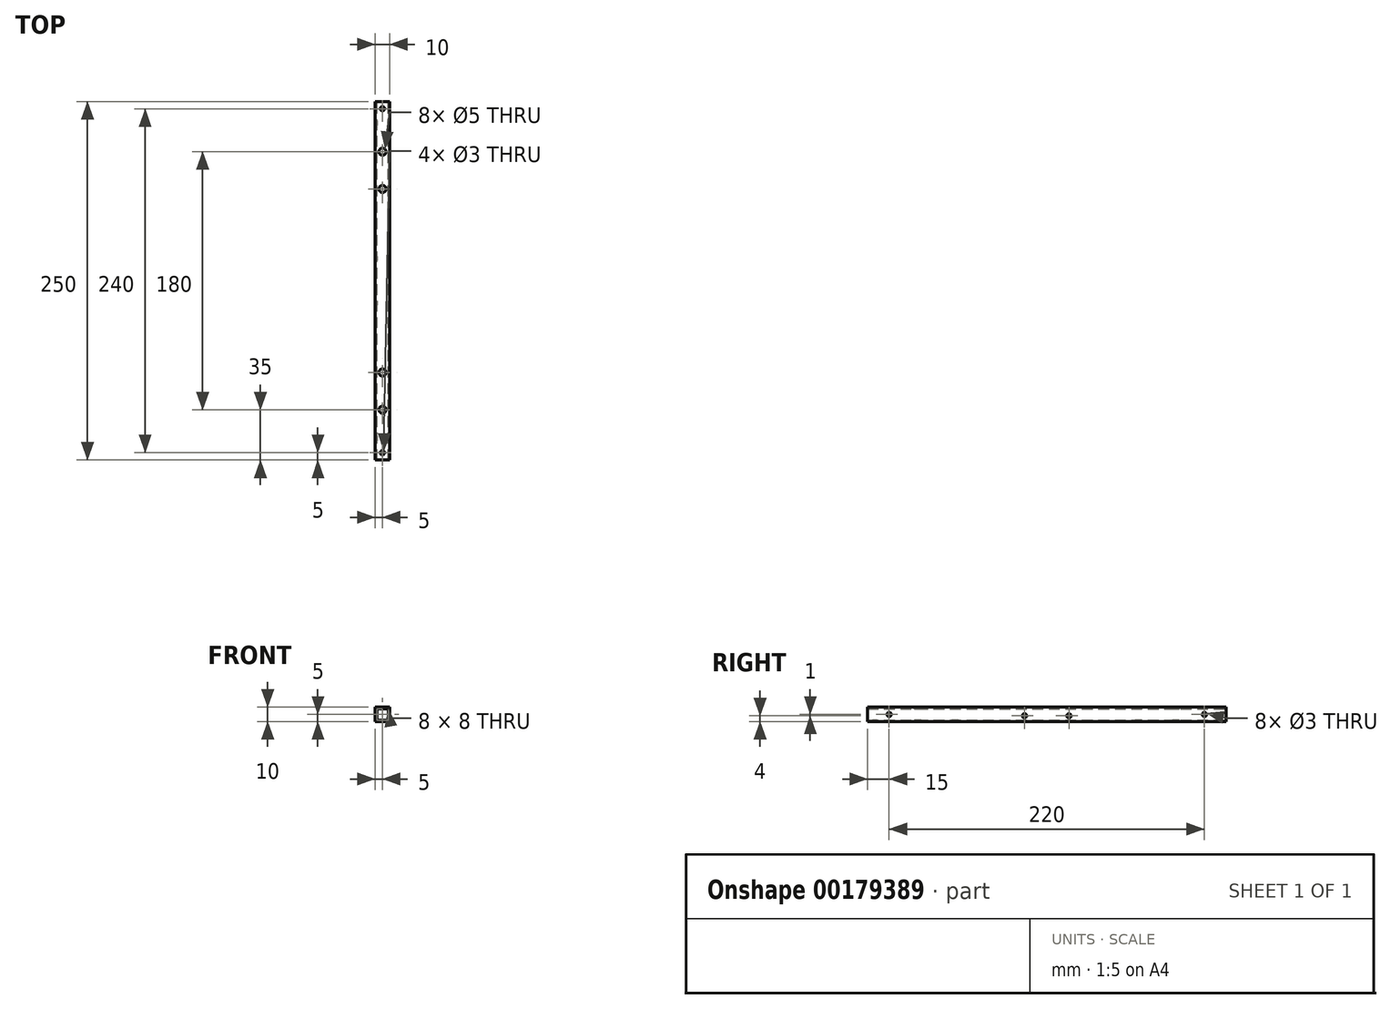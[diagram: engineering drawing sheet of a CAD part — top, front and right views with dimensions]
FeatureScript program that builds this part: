
annotation { "Feature Type Name" : "Feature", "Feature Type Description" : "" }
export const myFeature = defineFeature(function(context is Context, id is Id, definition is map)
    precondition{}
    {
        {
            var Q0;
            Q0=qCreatedBy(makeId("Front.planeOp"),FACE);
            var sketch = newSketch(context, id + "F0", { "sketchPlane" : qUnion([Q0])});
            skLineSegment(sketch, "E0.bottom", {"start": v(-5, -5) * mm, "end": v(5, -5) * mm});
            skLineSegment(sketch, "E0.top", {"start": v(-5, 5) * mm, "end": v(5, 5) * mm});
            skLineSegment(sketch, "E0.left", {"start": v(-5, -5) * mm, "end": v(-5, 5) * mm});
            skLineSegment(sketch, "E0.right", {"start": v(5, -5) * mm, "end": v(5, 5) * mm});
            skPoint(sketch, "E0.middle", {"position": v(0, 0) * mm});
            skLineSegment(sketch, "E1.bottom", {"start": v(-4, -4) * mm, "end": v(4, -4) * mm});
            skLineSegment(sketch, "E1.top", {"start": v(-4, 4) * mm, "end": v(4, 4) * mm});
            skLineSegment(sketch, "E1.left", {"start": v(-4, -4) * mm, "end": v(-4, 4) * mm});
            skLineSegment(sketch, "E1.right", {"start": v(4, -4) * mm, "end": v(4, 4) * mm});
            skSolve(sketch);
        }
        {
            var Q0;
            Q0=qSketchRegion(id+"F0",true);
            extrude(context, id + "F1", {"entities" : qUnion([Q0]), "depth" : 250 * mm});
        }
        {
            var Q0;
            Q0=makeQuery(id+"F1.opExtrude","SWEPT_FACE",FACE,{"disambiguationData":[OSD([sQuery(id+"F0.wireOp",EDGE,"E0.right")])]});
            var sketch = newSketch(context, id + "F2", { "sketchPlane" : qUnion([Q0])});
            skLineSegment(sketch, "E2", {"start": v(-125, 5) * mm, "end": v(-125, -5) * mm, "construction": true});
            skLineSegment(sketch, "E3.MirrorCS", {"start": v(0, -1) * mm, "end": v(-250, -1) * mm, "construction": true});
            skCircle(sketch, "E4", {"center": v(-140.5, -1) * mm, "radius": 1.5 * mm});
            skCircle(sketch, "E5.MirrorC", {"center": v(-109.5, -1) * mm, "radius": 1.5 * mm});
            skLineSegment(sketch, "E6", {"start": v(-250, 0) * mm, "end": v(0, 0) * mm, "construction": true});
            skCircle(sketch, "E7", {"center": v(-235, 0) * mm, "radius": 1.5 * mm});
            skCircle(sketch, "E8.MirrorC", {"center": v(-15, 0) * mm, "radius": 1.5 * mm});
            skSolve(sketch);
        }
        {
            var Q0;
            Q0=makeQuery(id+"F1.opExtrude","SWEPT_FACE",FACE,{"disambiguationData":[OSD([sQuery(id+"F0.wireOp",EDGE,"E0.top")])]});
            var sketch = newSketch(context, id + "F3", { "sketchPlane" : qUnion([Q0])});
            skLineSegment(sketch, "E9", {"start": v(0, 0) * mm, "end": v(0, -250) * mm, "construction": true});
            skLineSegment(sketch, "E10", {"start": v(5, -125) * mm, "end": v(-5, -125) * mm, "construction": true});
            skCircle(sketch, "E11", {"center": v(0, -245) * mm, "radius": 1.5 * mm});
            skCircle(sketch, "E12.MirrorC", {"center": v(0, -5) * mm, "radius": 1.5 * mm});
            skCircle(sketch, "E13", {"center": v(0, -215) * mm, "radius": 2.5 * mm});
            skCircle(sketch, "E14", {"center": v(0, -189) * mm, "radius": 2.5 * mm});
            skCircle(sketch, "E15.MirrorC", {"center": v(0, -61) * mm, "radius": 2.5 * mm});
            skCircle(sketch, "E16.MirrorC", {"center": v(0, -35) * mm, "radius": 2.5 * mm});
            skSolve(sketch);
        }
        {
            var Q0;
            Q0=qSketchRegion(id+"F2",true);
            extrude(context, id + "F4", {"entities" : qUnion([Q0]), "operationType" : NewBodyOperationType.REMOVE, "oppositeDirection" : true, "depth" : 25 * mm});
        }
        {
            var Q0;
            Q0=qSketchRegion(id+"F3",true);
            extrude(context, id + "F5", {"entities" : qUnion([Q0]), "operationType" : NewBodyOperationType.REMOVE, "oppositeDirection" : true, "depth" : 25 * mm});
        }
    });
